# Revit family: 414130001 DH SEN CTA BALTA
name_source: partatom
category: Plumbing Fixtures
units: mm (PartAtom-declared; Revit-internal decimal feet)

## family parameters
Always vertical = Yes
Cut with Voids When Loaded = No
Host = Wall
OmniClass Number = 23.31.11.17.15
OmniClass Title = Shower Disc Faucets
Part Type = Normal
Room Calculation Point = No
Round Connector Dimension = Use Diameter
Shared = No

## types (1)
- BALTA
    Acometidas = 1/2-14 NPT.
    Alto = 861.68 mm
    Altura MD = 800 mm  [stored 2.62467 ft]
    Altura ducha = 2000 mm  [stored 6.56168 ft]
    Altura mezclador = 1200 mm
    Ancho = 310 mm
    Capacidad de flujo máximo a 80 psi = 9,5 L/min
    Ciclo de vida de la unidad de cierre = 250.000 ciclos
    Creado por = IDD
    Description = La ducha sencilla BALTA, ha sido diseñada para trabajar en perfecta armonía con el espacio; inspirada en
las necesidades del consumidor latinoamericano dando como resultado un producto robusto y funcional.
Ideal para instalaciones donde no se necesita mezclar agua fría y caliente. Incorpora un sistema aireador
que genera un chorro de agua espumoso, agradable al tacto.• Grifería de Ducha con ahorro de agua.
• Brazo con mayor longitud que permite mayor alcance dando confort en el uso.
• Fácil limpieza: Diseño que evita la acumulación de impurezas.
• Regadera con funciones dando confort en el uso.
    Fabricante = Corona
    Fecha de creación = 21/07/2020
    Garantía = 30 años
    Garantía Cromado = 5 años
    Manufacturer = Corona
    Material = Corona_Cromado
    Model = DUCHA SENCILLA BALTA
    Peso Bruto aprox = 675 gr. 1,49 lb.
    Peso Neto aprox = 525 gr. 1,16 lb.
    Presión máxima recomendada = 125 psi (862 Kpa)
    Presión mínima recomendada = 20 psi (138 Kpa)
    Profundidad = 320 mm  [stored 1.04987 ft]
    Rango de temperatura máxima de funcionamiento = 5ºC a 71ºC.
    Referencia = 414130001
    Vida útil de la junta de bola (Regadera) = 10.000 ciclos
    Vida útil de la unidad de cierre (unidad) = 250.000 ciclos.

note: [stored X ft] marks values corroborated as IEEE doubles in the binary element streams (Revit-internal decimal feet)

## geometry (parser evidence)
native form markers: Sweep x13
no freeform markers — native parametric forms only
